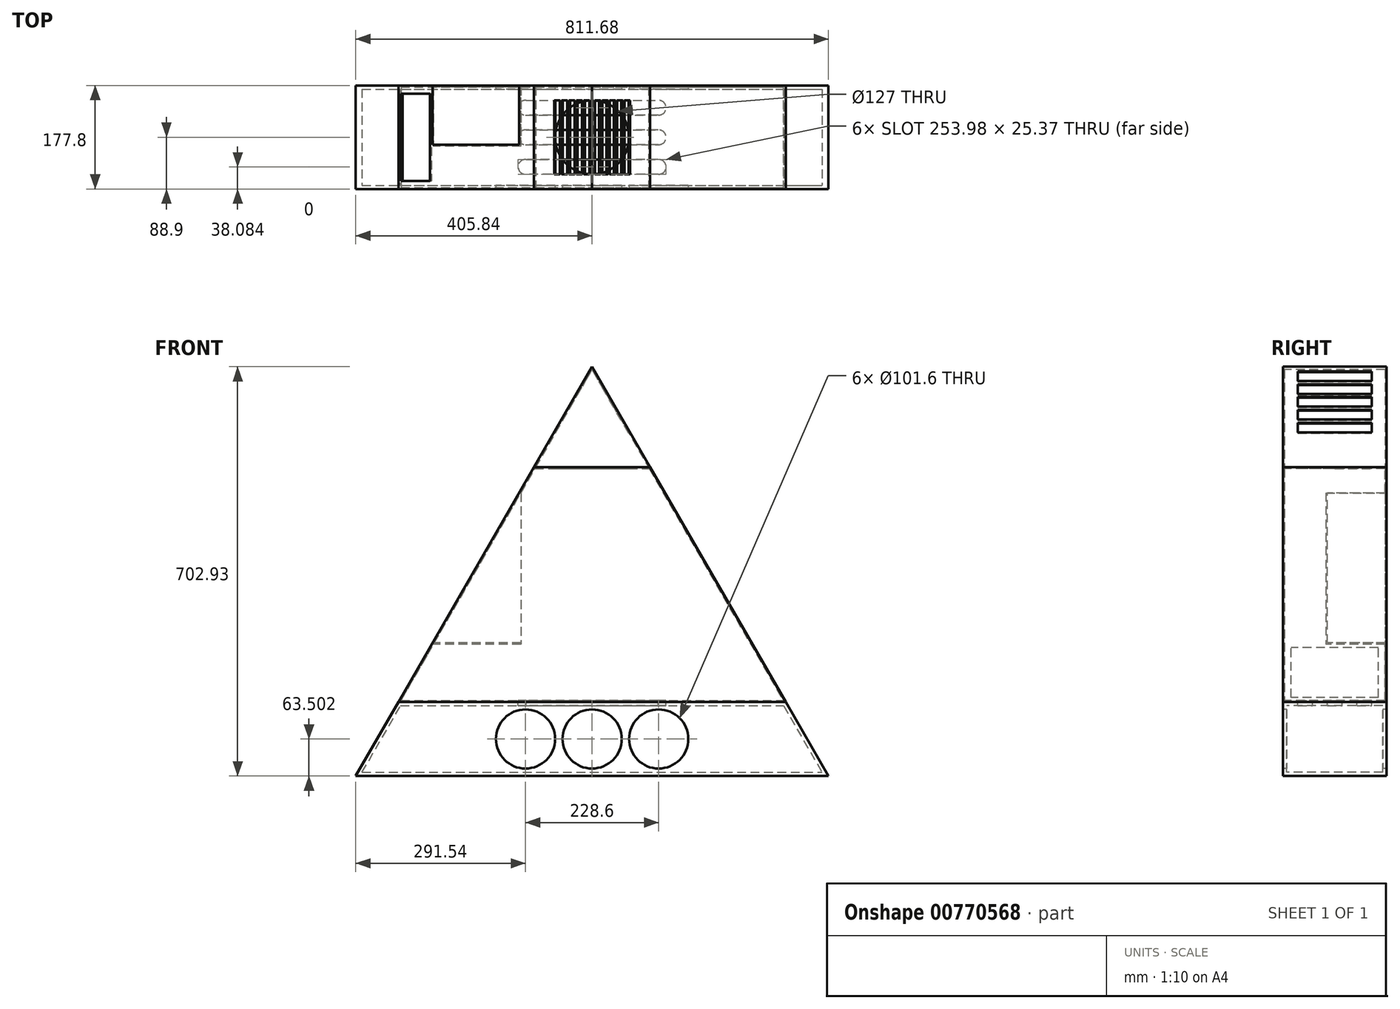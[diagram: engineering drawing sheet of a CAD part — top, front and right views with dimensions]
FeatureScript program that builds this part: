
annotation { "Feature Type Name" : "Feature", "Feature Type Description" : "" }
export const myFeature = defineFeature(function(context is Context, id is Id, definition is map)
    precondition{}
    {
        {
            var Q0;
            Q0=qCreatedBy(makeId("Front.planeOp"),FACE);
            var sketch = newSketch(context, id + "F0", { "sketchPlane" : qUnion([Q0])});
            skLineSegment(sketch, "E0.bottom", {"start": v(122.24, 122.24) * mm, "end": v(-122.24, 122.24) * mm, "construction": true});
            skLineSegment(sketch, "E0.top", {"start": v(122.24, -122.24) * mm, "end": v(-122.24, -122.24) * mm, "construction": true});
            skLineSegment(sketch, "E0.left", {"start": v(122.24, 122.24) * mm, "end": v(122.24, -122.24) * mm, "construction": true});
            skLineSegment(sketch, "E0.right", {"start": v(-122.24, 122.24) * mm, "end": v(-122.24, -122.24) * mm, "construction": true});
            skPoint(sketch, "E0.middle", {"position": v(0, 0) * mm});
            skLineSegment(sketch, "E1.1", {"start": v(-405.84, -357.19) * mm, "end": v(0, 345.74) * mm});
            skLineSegment(sketch, "E1.2", {"start": v(0, 345.74) * mm, "end": v(405.84, -357.19) * mm});
            skPoint(sketch, "E1.0.midPoint", {"position": v(0, -230.19) * mm});
            skLineSegment(sketch, "E2.top", {"start": v(-405.84, -357.19) * mm, "end": v(405.84, -357.19) * mm});
            skPoint(sketch, "E3.orphan", {"position": v(332.51, -230.19) * mm});
            skPoint(sketch, "E4.orphan", {"position": v(-332.51, -230.19) * mm});
            skLineSegment(sketch, "E5", {"start": v(-332.51, -230.19) * mm, "end": v(332.51, -230.19) * mm});
            skLineSegment(sketch, "E6", {"start": v(0, -230.19) * mm, "end": v(0, -357.19) * mm, "construction": true});
            skPoint(sketch, "E7", {"position": v(0, 172.87) * mm});
            skLineSegment(sketch, "E8", {"start": v(-99.8, 172.87) * mm, "end": v(99.8, 172.87) * mm});
            skLineSegment(sketch, "E9", {"start": v(0, -122.24) * mm, "end": v(0, -230.19) * mm, "construction": true});
            skLineSegment(sketch, "E10", {"start": v(-122.24, 122.24) * mm, "end": v(-122.24, 134.02) * mm, "construction": true});
            skLineSegment(sketch, "E11", {"start": v(122.24, 122.24) * mm, "end": v(122.24, 134.02) * mm, "construction": true});
            skSolve(sketch);
        }
        {
            var Q0;
            {var subQ3=sQuery(id+"F0.wireOp",EDGE,"E5");Q0=makeQuery(id+"F0.imprint","IMPRINT",FACE,{"disambiguationData":[TD([[makeQuery(id+"F0.imprint","IMPRINT",EDGE,{"derivedFrom":subQ3}),1.0]])]});}
            var sketch = newSketch(context, id + "F1", { "sketchPlane" : qUnion([Q0])});
            skLineSegment(sketch, "E12.0", {"start": v(-122.24, 128.59) * mm, "end": v(-125.37, 128.59) * mm});
            skLineSegment(sketch, "E12.2", {"start": v(-122.24, -128.59) * mm, "end": v(-273.85, -128.59) * mm});
            skLineSegment(sketch, "E13.0", {"start": v(125.37, 128.59) * mm, "end": v(405.84, -357.19) * mm});
            skLineSegment(sketch, "E14.0", {"start": v(-122.24, 128.59) * mm, "end": v(-122.24, -128.59) * mm});
            skPoint(sketch, "E15.orphan", {"position": v(-122.24, 122.24) * mm});
            skPoint(sketch, "E16.orphan", {"position": v(-122.24, -122.24) * mm});
            skPoint(sketch, "E17.orphan", {"position": v(-405.84, -357.19) * mm});
            skLineSegment(sketch, "E18.0", {"start": v(-332.51, -230.19) * mm, "end": v(332.51, -230.19) * mm});
            skLineSegment(sketch, "E19.0", {"start": v(-405.84, -357.19) * mm, "end": v(-273.85, -128.59) * mm});
            skPoint(sketch, "E20.orphan", {"position": v(0, 345.74) * mm});
            skPoint(sketch, "E21.0", {"position": v(-99.8, 172.87) * mm});
            skPoint(sketch, "E22.0", {"position": v(99.8, 172.87) * mm});
            skLineSegment(sketch, "E23", {"start": v(-125.37, 128.59) * mm, "end": v(-99.8, 172.87) * mm});
            skLineSegment(sketch, "E24", {"start": v(-99.8, 172.87) * mm, "end": v(99.8, 172.87) * mm});
            skLineSegment(sketch, "E25", {"start": v(99.8, 172.87) * mm, "end": v(125.37, 128.59) * mm});
            skSolve(sketch);
        }
        {
            var Q0;
            Q0 = qSketchRegion(id + "F1", true);
            extrude(context, id + "F2", {"entities" : qUnion([Q0]), "oppositeDirection" : true, "depth" : 101.6 * mm, "offsetDistance" : 25.4 * mm});
        }
        {
            var Q0;
            {var subQ0=sQuery(id+"F0.wireOp",EDGE,"E5");Q0=makeQuery(id+"F0.imprint","IMPRINT",FACE,{"disambiguationData":[TD([[makeQuery(id+"F0.imprint","IMPRINT",EDGE,{"derivedFrom":subQ0}),1.0]])]});}
            extrude(context, id + "F3", {"entities" : qUnion([Q0]), "operationType" : NewBodyOperationType.ADD, "depth" : 76.2 * mm, "offsetDistance" : 25.4 * mm});
        }
        {
            var Q0;
            {var subQ0=sQuery(id+"F0.wireOp",EDGE,"E2.top");Q0=makeQuery(id+"F0.imprint","IMPRINT",FACE,{"disambiguationData":[TD([[makeQuery(id+"F0.imprint","IMPRINT",EDGE,{"derivedFrom":subQ0}),1.0]])]});}
            var Q1;
            Q1=makeQuery(id+"F2.opExtrude","CAP_VERTEX",VERTEX,{"disambiguationData":[OSD([sQuery(id+"F1.wireOp",EDGE,"E13.0"),sQuery(id+"F1.wireOp",EDGE,"E18.0")])],"isStart":false});
            var Q2;
            Q2=makeQuery(id+"F3.opExtrude","CAP_VERTEX",VERTEX,{"disambiguationData":[OSD([sQuery(id+"F0.wireOp",EDGE,"E1.2"),sQuery(id+"F0.wireOp",EDGE,"E5")])],"isStart":false});
            extrude(context, id + "F4", {"entities" : qUnion([Q0]), "endBound" : BoundingType.UP_TO_VERTEX, "oppositeDirection" : true, "depth" : 25.4 * mm, "endBoundEntityVertex" : qUnion([Q1]), "offsetDistance" : 25.4 * mm, "hasSecondDirection" : true, "secondDirectionBound" : SecondDirectionBoundingType.UP_TO_VERTEX, "secondDirectionOppositeDirection" : false, "secondDirectionDepth" : 25.4 * mm, "secondDirectionBoundEntityVertex" : qUnion([Q2])});
        }
        {
            var Q0;
            Q0=makeQuery(id+"F2.opExtrude","SWEPT_FACE",FACE,{"disambiguationData":[OSD([sQuery(id+"F1.wireOp",EDGE,"E14.0")])]});
            shell(context, id + "F5", {"entities" : qUnion([Q0]), "thickness" : 2.54 * mm});
        }
        {
            var Q0;
            {var subQ3=sQuery(id+"F0.wireOp",EDGE,"E8");Q0=makeQuery(id+"F0.imprint","IMPRINT",FACE,{"disambiguationData":[TD([[makeQuery(id+"F0.imprint","IMPRINT",EDGE,{"derivedFrom":subQ3}),1.0]])]});}
            var Q1;
            Q1=makeQuery(id+"F2.opExtrude","CAP_VERTEX",VERTEX,{"disambiguationData":[OSD([sQuery(id+"F1.wireOp",EDGE,"E23"),sQuery(id+"F1.wireOp",EDGE,"E24")])],"isStart":false});
            var Q2;
            Q2=makeQuery(id+"F3.opExtrude","CAP_VERTEX",VERTEX,{"disambiguationData":[OSD([sQuery(id+"F0.wireOp",EDGE,"E1.1"),sQuery(id+"F0.wireOp",EDGE,"E8")])],"isStart":false});
            extrude(context, id + "F6", {"entities" : qUnion([Q0]), "endBound" : BoundingType.UP_TO_VERTEX, "oppositeDirection" : true, "depth" : 25.4 * mm, "endBoundEntityVertex" : qUnion([Q1]), "offsetDistance" : 25.4 * mm, "hasSecondDirection" : true, "secondDirectionBound" : SecondDirectionBoundingType.UP_TO_VERTEX, "secondDirectionOppositeDirection" : false, "secondDirectionDepth" : 25.4 * mm, "secondDirectionBoundEntityVertex" : qUnion([Q2])});
        }
        {
            var Q0;
            {var subQ0=sQuery(id+"F0.wireOp",EDGE,"E1.1");Q0=qUnion([makeQuery(id+"F3.boolean.opBoolean","MERGE",FACE,{"derivedFrom":[makeQuery(id+"F2.opExtrude","SWEPT_FACE",FACE,{"disambiguationData":[OSD([sQuery(id+"F1.wireOp",EDGE,"E19.0")])]}),makeQuery(id+"F2.opExtrude","SWEPT_FACE",FACE,{"disambiguationData":[OSD([sQuery(id+"F1.wireOp",EDGE,"E23")])]}),makeQuery(id+"F3.opExtrude","SWEPT_FACE",FACE,{"disambiguationData":[OSD([subQ0])]})]}),makeQuery(id+"F6.opExtrude","SWEPT_FACE",FACE,{"disambiguationData":[OSD([subQ0])]})]);}
            var sketch = newSketch(context, id + "F7", { "sketchPlane" : qUnion([Q0])});
            skLineSegment(sketch, "E26", {"start": v(-12.7, 299.42) * mm, "end": v(-12.7, 261.32) * mm, "construction": true});
            skLineSegment(sketch, "E27.bottom", {"start": v(50.8, 289.9) * mm, "end": v(-76.2, 289.9) * mm});
            skLineSegment(sketch, "E27.top", {"start": v(50.8, 270.84) * mm, "end": v(-76.2, 270.84) * mm});
            skLineSegment(sketch, "E27.left", {"start": v(50.8, 289.9) * mm, "end": v(50.8, 270.84) * mm});
            skLineSegment(sketch, "E27.right", {"start": v(-76.2, 289.9) * mm, "end": v(-76.2, 270.84) * mm});
            skPoint(sketch, "E27.middle", {"position": v(-12.7, 280.37) * mm});
            skLineSegment(sketch, "E28.0.1.0", {"start": v(-76.2, 264.5) * mm, "end": v(-76.2, 245.44) * mm});
            skLineSegment(sketch, "E28.0.1.1", {"start": v(50.8, 264.5) * mm, "end": v(-76.2, 264.5) * mm});
            skLineSegment(sketch, "E28.0.1.2", {"start": v(50.8, 245.44) * mm, "end": v(-76.2, 245.44) * mm});
            skLineSegment(sketch, "E28.0.1.3", {"start": v(50.8, 264.5) * mm, "end": v(50.8, 245.44) * mm});
            skLineSegment(sketch, "E28.0.2.0", {"start": v(-76.2, 239.1) * mm, "end": v(-76.2, 220.04) * mm});
            skLineSegment(sketch, "E28.0.2.1", {"start": v(50.8, 239.1) * mm, "end": v(-76.2, 239.1) * mm});
            skLineSegment(sketch, "E28.0.2.2", {"start": v(50.8, 220.04) * mm, "end": v(-76.2, 220.04) * mm});
            skLineSegment(sketch, "E28.0.2.3", {"start": v(50.8, 239.1) * mm, "end": v(50.8, 220.04) * mm});
            skLineSegment(sketch, "E28.0.3.0", {"start": v(-76.2, 213.7) * mm, "end": v(-76.2, 194.64) * mm});
            skLineSegment(sketch, "E28.0.3.1", {"start": v(50.8, 213.7) * mm, "end": v(-76.2, 213.7) * mm});
            skLineSegment(sketch, "E28.0.3.2", {"start": v(50.8, 194.64) * mm, "end": v(-76.2, 194.64) * mm});
            skLineSegment(sketch, "E28.0.3.3", {"start": v(50.8, 213.7) * mm, "end": v(50.8, 194.64) * mm});
            skLineSegment(sketch, "E28.0.4.0", {"start": v(-76.2, 188.3) * mm, "end": v(-76.2, 169.24) * mm});
            skLineSegment(sketch, "E28.0.4.1", {"start": v(50.8, 188.3) * mm, "end": v(-76.2, 188.3) * mm});
            skLineSegment(sketch, "E28.0.4.2", {"start": v(50.8, 169.24) * mm, "end": v(-76.2, 169.24) * mm});
            skLineSegment(sketch, "E28.0.4.3", {"start": v(50.8, 188.3) * mm, "end": v(50.8, 169.24) * mm});
            skLineSegment(sketch, "E28.direction1", {"start": v(-76.2, 270.84) * mm, "end": v(-44.45, 270.84) * mm, "construction": true});
            skLineSegment(sketch, "E28.direction2", {"start": v(-76.2, 270.84) * mm, "end": v(-76.2, 245.44) * mm, "construction": true});
            skSolve(sketch);
        }
        {
            var Q0;
            {var subQ0=sQuery(id+"F0.wireOp",EDGE,"E1.2");Q0=qUnion([makeQuery(id+"F3.boolean.opBoolean","MERGE",FACE,{"derivedFrom":[makeQuery(id+"F2.opExtrude","SWEPT_FACE",FACE,{"disambiguationData":[OSD([sQuery(id+"F1.wireOp",EDGE,"E13.0"),sQuery(id+"F1.wireOp",EDGE,"E25")])]}),makeQuery(id+"F3.opExtrude","SWEPT_FACE",FACE,{"disambiguationData":[OSD([subQ0])]})]}),makeQuery(id+"F6.opExtrude","SWEPT_FACE",FACE,{"disambiguationData":[OSD([subQ0])]})]);}
            var sketch = newSketch(context, id + "F8", { "sketchPlane" : qUnion([Q0])});
            skLineSegment(sketch, "E29", {"start": v(12.7, 299.42) * mm, "end": v(12.7, 261.32) * mm, "construction": true});
            skLineSegment(sketch, "E30.bottom", {"start": v(76.2, 289.9) * mm, "end": v(-50.8, 289.9) * mm});
            skLineSegment(sketch, "E30.top", {"start": v(76.2, 270.84) * mm, "end": v(-50.8, 270.84) * mm});
            skLineSegment(sketch, "E30.left", {"start": v(76.2, 289.9) * mm, "end": v(76.2, 270.84) * mm});
            skLineSegment(sketch, "E30.right", {"start": v(-50.8, 289.9) * mm, "end": v(-50.8, 270.84) * mm});
            skPoint(sketch, "E30.middle", {"position": v(12.7, 280.37) * mm});
            skLineSegment(sketch, "E31.0.1.0", {"start": v(-50.8, 264.5) * mm, "end": v(-50.8, 245.44) * mm});
            skLineSegment(sketch, "E31.0.1.1", {"start": v(76.2, 264.5) * mm, "end": v(-50.8, 264.5) * mm});
            skLineSegment(sketch, "E31.0.1.2", {"start": v(76.2, 245.44) * mm, "end": v(-50.8, 245.44) * mm});
            skLineSegment(sketch, "E31.0.1.3", {"start": v(76.2, 264.5) * mm, "end": v(76.2, 245.44) * mm});
            skLineSegment(sketch, "E31.0.2.0", {"start": v(-50.8, 239.1) * mm, "end": v(-50.8, 220.04) * mm});
            skLineSegment(sketch, "E31.0.2.1", {"start": v(76.2, 239.1) * mm, "end": v(-50.8, 239.1) * mm});
            skLineSegment(sketch, "E31.0.2.2", {"start": v(76.2, 220.04) * mm, "end": v(-50.8, 220.04) * mm});
            skLineSegment(sketch, "E31.0.2.3", {"start": v(76.2, 239.1) * mm, "end": v(76.2, 220.04) * mm});
            skLineSegment(sketch, "E31.0.3.0", {"start": v(-50.8, 213.7) * mm, "end": v(-50.8, 194.64) * mm});
            skLineSegment(sketch, "E31.0.3.1", {"start": v(76.2, 213.7) * mm, "end": v(-50.8, 213.7) * mm});
            skLineSegment(sketch, "E31.0.3.2", {"start": v(76.2, 194.64) * mm, "end": v(-50.8, 194.64) * mm});
            skLineSegment(sketch, "E31.0.3.3", {"start": v(76.2, 213.7) * mm, "end": v(76.2, 194.64) * mm});
            skLineSegment(sketch, "E31.0.4.0", {"start": v(-50.8, 188.3) * mm, "end": v(-50.8, 169.24) * mm});
            skLineSegment(sketch, "E31.0.4.1", {"start": v(76.2, 188.3) * mm, "end": v(-50.8, 188.3) * mm});
            skLineSegment(sketch, "E31.0.4.2", {"start": v(76.2, 169.24) * mm, "end": v(-50.8, 169.24) * mm});
            skLineSegment(sketch, "E31.0.4.3", {"start": v(76.2, 188.3) * mm, "end": v(76.2, 169.24) * mm});
            skLineSegment(sketch, "E31.direction1", {"start": v(-50.8, 270.84) * mm, "end": v(57.15, 270.84) * mm, "construction": true});
            skLineSegment(sketch, "E31.direction2", {"start": v(-50.8, 270.84) * mm, "end": v(-50.8, 245.44) * mm, "construction": true});
            skSolve(sketch);
        }
        {
            var Q0;
            Q0=makeQuery(id+"F6.opExtrude","SWEPT_FACE",FACE,{"disambiguationData":[OSD([sQuery(id+"F0.wireOp",EDGE,"E8")])]});
            shell(context, id + "F9", {"entities" : qUnion([Q0]), "thickness" : 2.54 * mm});
        }
        {
            var Q0;
            Q0 = qSketchRegion(id + "F7", true);
            extrude(context, id + "F10", {"entities" : qUnion([Q0]), "operationType" : NewBodyOperationType.REMOVE, "oppositeDirection" : true, "depth" : 12.7 * mm, "offsetDistance" : 25.4 * mm});
        }
        {
            var Q0;
            Q0=makeQuery(id+"F4.opExtrude","CAP_FACE",FACE,{"disambiguationData":[OSD([sQuery(id+"F0.wireOp",EDGE,"E1.1"),sQuery(id+"F0.wireOp",EDGE,"E1.2"),sQuery(id+"F0.wireOp",EDGE,"E2.top"),sQuery(id+"F0.wireOp",EDGE,"E5")])],"isStart":false});
            var Q1;
            Q1=makeQuery(id+"F4.opExtrude","SWEPT_BODY",BODY,{"disambiguationData":[OSD([sQuery(id+"F0.wireOp",EDGE,"E1.1"),sQuery(id+"F0.wireOp",EDGE,"E1.2"),sQuery(id+"F0.wireOp",EDGE,"E2.top"),sQuery(id+"F0.wireOp",EDGE,"E5")])]});
            shell(context, id + "F11", {"isHollow" : true, "entities" : qUnion([Q0]), "parts" : qUnion([Q1]), "thickness" : 6.35 * mm});
        }
        {
            var Q0;
            {var subQ0=sQuery(id+"F0.wireOp",EDGE,"E5");var subQ1=sQuery(id+"F0.wireOp",EDGE,"E2.top");var subQ2=sQuery(id+"F0.wireOp",EDGE,"E1.2");var subQ3=sQuery(id+"F0.wireOp",EDGE,"E1.1");Q0=makeQuery(id+"F11.opShell","OFFSET_FACE",FACE,{"disambiguationData":[OSD([subQ3,subQ2,subQ1,subQ0]),TDD([makeQuery(id+"F4.opExtrude","CAP_FACE",FACE,{"disambiguationData":[OSD([subQ3,subQ2,subQ1,subQ0])],"isStart":true})])]});}
            var sketch = newSketch(context, id + "F12", { "sketchPlane" : qUnion([Q0])});
            skLineSegment(sketch, "E32", {"start": v(0, -236.54) * mm, "end": v(0, -350.84) * mm, "construction": true});
            skCircle(sketch, "E33", {"center": v(0, -293.69) * mm, "radius": 50.8 * mm});
            skLineSegment(sketch, "E34.direction1", {"start": v(0, -293.69) * mm, "end": v(228.6, -293.69) * mm, "construction": true});
            skLineSegment(sketch, "E35", {"start": v(0, -293.69) * mm, "end": v(-231.4, -293.69) * mm, "construction": true});
            skCircle(sketch, "E36", {"center": v(114.3, -293.69) * mm, "radius": 50.8 * mm});
            skCircle(sketch, "E37", {"center": v(-114.3, -293.69) * mm, "radius": 50.8 * mm});
            skSolve(sketch);
        }
        {
            var Q0;
            Q0 = qSketchRegion(id + "F12", true);
            extrude(context, id + "F13", {"entities" : qUnion([Q0]), "operationType" : NewBodyOperationType.REMOVE, "endBound" : BoundingType.THROUGH_ALL, "depth" : 25.4 * mm, "offsetDistance" : 25.4 * mm, "hasSecondDirection" : true, "secondDirectionOppositeDirection" : true, "secondDirectionDepth" : 25.4 * mm});
        }
        {
            var Q0;
            Q0=makeQuery(id+"F5.opShell","OFFSET_FACE",FACE,{"disambiguationData":[OSD([sQuery(id+"F0.wireOp",EDGE,"E5"),sQuery(id+"F1.wireOp",EDGE,"E18.0")])]});
            var sketch = newSketch(context, id + "F14", { "sketchPlane" : qUnion([Q0])});
            skPoint(sketch, "E38", {"position": v(114.3, -50.8) * mm});
            skArc(sketch, "E39.0.startCap", {"start": v(-114.3, -50.8) * mm, "mid": v(-127, -37.65) * mm, "end": v(-113.4, -25.43) * mm});
            skLineSegment(sketch, "E39.0.endCap", {"start": v(114.3, -50.8) * mm, "end": v(114.3, -50.8) * mm});
            skLineSegment(sketch, "E39.0.right", {"start": v(-114.3, -50.8) * mm, "end": v(114.3, -50.8) * mm});
            skLineSegment(sketch, "E40", {"start": v(0, -50.8) * mm, "end": v(0, 101.6) * mm, "construction": true});
            skArc(sketch, "E41.MirrorCS", {"start": v(114.3, -50.8) * mm, "mid": v(127, -37.65) * mm, "end": v(113.4, -25.43) * mm});
            skLineSegment(sketch, "E42", {"start": v(113.4, -25.43) * mm, "end": v(-113.4, -25.43) * mm});
            skLineSegment(sketch, "E43.0.1.0", {"start": v(-114.3, 0) * mm, "end": v(114.3, 0) * mm});
            skLineSegment(sketch, "E43.0.1.1", {"start": v(113.4, 25.37) * mm, "end": v(-113.4, 25.37) * mm});
            skArc(sketch, "E43.0.1.2", {"start": v(-114.3, 0) * mm, "mid": v(-127, 13.15) * mm, "end": v(-113.4, 25.37) * mm});
            skArc(sketch, "E43.0.1.3", {"start": v(114.3, 0) * mm, "mid": v(127, 13.15) * mm, "end": v(113.4, 25.37) * mm});
            skLineSegment(sketch, "E43.0.2.0", {"start": v(-114.3, 50.8) * mm, "end": v(114.3, 50.8) * mm});
            skLineSegment(sketch, "E43.0.2.1", {"start": v(113.4, 76.17) * mm, "end": v(-113.4, 76.17) * mm});
            skArc(sketch, "E43.0.2.2", {"start": v(-114.3, 50.8) * mm, "mid": v(-127, 63.95) * mm, "end": v(-113.4, 76.17) * mm});
            skArc(sketch, "E43.0.2.3", {"start": v(114.3, 50.8) * mm, "mid": v(127, 63.95) * mm, "end": v(113.4, 76.17) * mm});
            skLineSegment(sketch, "E43.direction1", {"start": v(-114.3, -50.8) * mm, "end": v(-88.9, -50.8) * mm, "construction": true});
            skLineSegment(sketch, "E43.direction2", {"start": v(-114.3, -50.8) * mm, "end": v(-114.3, 0) * mm, "construction": true});
            skSolve(sketch);
        }
        {
            var Q0;
            Q0 = qSketchRegion(id + "F14", true);
            extrude(context, id + "F15", {"entities" : qUnion([Q0]), "operationType" : NewBodyOperationType.REMOVE, "oppositeDirection" : true, "depth" : 25.4 * mm, "offsetDistance" : 25.4 * mm});
        }
        {
            var Q0;
            Q0 = qSketchRegion(id + "F8", true);
            extrude(context, id + "F16", {"entities" : qUnion([Q0]), "operationType" : NewBodyOperationType.REMOVE, "oppositeDirection" : true, "depth" : 12.7 * mm, "offsetDistance" : 25.4 * mm});
        }
        {
            var Q0;
            Q0=makeQuery(id+"F3.boolean.opBoolean","MERGE",FACE,{"derivedFrom":[makeQuery(id+"F2.opExtrude","SWEPT_FACE",FACE,{"disambiguationData":[OSD([sQuery(id+"F1.wireOp",EDGE,"E24")])]}),makeQuery(id+"F3.opExtrude","SWEPT_FACE",FACE,{"disambiguationData":[OSD([sQuery(id+"F0.wireOp",EDGE,"E8")])]})]});
            var sketch = newSketch(context, id + "F17", { "sketchPlane" : qUnion([Q0])});
            skLineSegment(sketch, "E44", {"start": v(0, -76.2) * mm, "end": v(0, 101.6) * mm, "construction": true});
            skCircle(sketch, "E45", {"center": v(0, 12.7) * mm, "radius": 63.5 * mm});
            skSolve(sketch);
        }
        {
            var Q0;
            Q0 = qSketchRegion(id + "F17", true);
            extrude(context, id + "F18", {"entities" : qUnion([Q0]), "operationType" : NewBodyOperationType.REMOVE, "oppositeDirection" : true, "depth" : 25.4 * mm, "offsetDistance" : 25.4 * mm});
        }
        {
            var Q0;
            Q0=makeQuery(id+"F3.boolean.opBoolean","MERGE",EDGE,{"derivedFrom":[makeQuery(id+"F2.opExtrude","SWEPT_EDGE",EDGE,{"disambiguationData":[OSD([sQuery(id+"F1.wireOp",EDGE,"E18.0"),sQuery(id+"F1.wireOp",EDGE,"E19.0")])]}),makeQuery(id+"F3.opExtrude","SWEPT_EDGE",EDGE,{"disambiguationData":[OSD([sQuery(id+"F0.wireOp",EDGE,"E1.1"),sQuery(id+"F0.wireOp",EDGE,"E5")])]})]});
            cPoint(context, id + "F19", {"entities" : qUnion([Q0]), "parameter" : 0.5});
        }
        {
            var Q0;
            Q0=qCreatedBy(makeId("Right.planeOp"),FACE);
            var Q1;
            Q1 = qCreatedBy(id + "F19" ,VERTEX);
            cPlane(context, id + "F20", {"entities" : qUnion([Q0, Q1]), "cplaneType" : CPlaneType.PLANE_POINT, "offset" : 25.4 * mm, "width" : 152.4 * mm, "height" : 152.4 * mm});
        }
        {
            var Q0;
            Q0=qCreatedBy(id+"F20.planeOp",FACE);
            var sketch = newSketch(context, id + "F21", { "sketchPlane" : qUnion([Q0])});
            skLineSegment(sketch, "E46.0", {"start": v(101.6, -230.19) * mm, "end": v(101.6, -128.59) * mm, "construction": true});
            skLineSegment(sketch, "E47.0", {"start": v(101.6, -230.19) * mm, "end": v(-76.2, -230.19) * mm, "construction": true});
            skLineSegment(sketch, "E48", {"start": v(101.6, -128.59) * mm, "end": v(-76.2, -230.19) * mm, "construction": true});
            skLineSegment(sketch, "E49.bottom", {"start": v(-62.23, -136.46) * mm, "end": v(87.63, -136.46) * mm});
            skLineSegment(sketch, "E49.top", {"start": v(-62.23, -222.31) * mm, "end": v(87.63, -222.31) * mm});
            skLineSegment(sketch, "E49.left", {"start": v(-62.23, -136.46) * mm, "end": v(-62.23, -222.31) * mm});
            skLineSegment(sketch, "E49.right", {"start": v(87.63, -136.46) * mm, "end": v(87.63, -222.31) * mm});
            skPoint(sketch, "E49.middle", {"position": v(12.7, -179.39) * mm});
            skSolve(sketch);
        }
        {
            var Q0;
            Q0=makeQuery(id+"F11.opShell","OFFSET_FACE",FACE,{"disambiguationData":[OSD([sQuery(id+"F0.wireOp",EDGE,"E5")])]});
            var sketch = newSketch(context, id + "F22", { "sketchPlane" : qUnion([Q0])});
            skLineSegment(sketch, "E50.0", {"start": v(114.3, 50.8) * mm, "end": v(-114.3, 50.8) * mm});
            skArc(sketch, "E51.0", {"start": v(-113.4, 25.43) * mm, "mid": v(-127, 37.65) * mm, "end": v(-114.3, 50.8) * mm});
            skLineSegment(sketch, "E52.0", {"start": v(-113.4, 25.43) * mm, "end": v(113.4, 25.43) * mm});
            skArc(sketch, "E53.0", {"start": v(113.4, 25.43) * mm, "mid": v(127, 37.65) * mm, "end": v(114.3, 50.8) * mm});
            skArc(sketch, "E54.0", {"start": v(113.4, -25.37) * mm, "mid": v(127, -13.15) * mm, "end": v(114.3, 0) * mm});
            skLineSegment(sketch, "E55.0", {"start": v(114.3, 0) * mm, "end": v(-114.3, 0) * mm});
            skLineSegment(sketch, "E56.0", {"start": v(-113.4, -25.37) * mm, "end": v(113.4, -25.37) * mm});
            skArc(sketch, "E57.0", {"start": v(-113.4, -25.37) * mm, "mid": v(-127, -13.15) * mm, "end": v(-114.3, 0) * mm});
            skArc(sketch, "E58.0", {"start": v(-113.4, -76.17) * mm, "mid": v(-127, -63.95) * mm, "end": v(-114.3, -50.8) * mm});
            skLineSegment(sketch, "E59.0", {"start": v(114.3, -50.8) * mm, "end": v(-114.3, -50.8) * mm});
            skLineSegment(sketch, "E60.0", {"start": v(-113.4, -76.17) * mm, "end": v(113.4, -76.17) * mm});
            skArc(sketch, "E61.0", {"start": v(113.4, -76.17) * mm, "mid": v(127, -63.95) * mm, "end": v(114.3, -50.8) * mm});
            skSolve(sketch);
        }
        {
            var Q0;
            Q0 = qSketchRegion(id + "F22", true);
            extrude(context, id + "F23", {"entities" : qUnion([Q0]), "operationType" : NewBodyOperationType.REMOVE, "oppositeDirection" : true, "depth" : 25.4 * mm, "offsetDistance" : 25.4 * mm});
        }
        {
            var Q0;
            Q0 = qSketchRegion(id + "F21", true);
            extrude(context, id + "F24", {"entities" : qUnion([Q0]), "operationType" : NewBodyOperationType.REMOVE, "depth" : 142.24 * mm, "offsetDistance" : 25.4 * mm});
        }
    });
